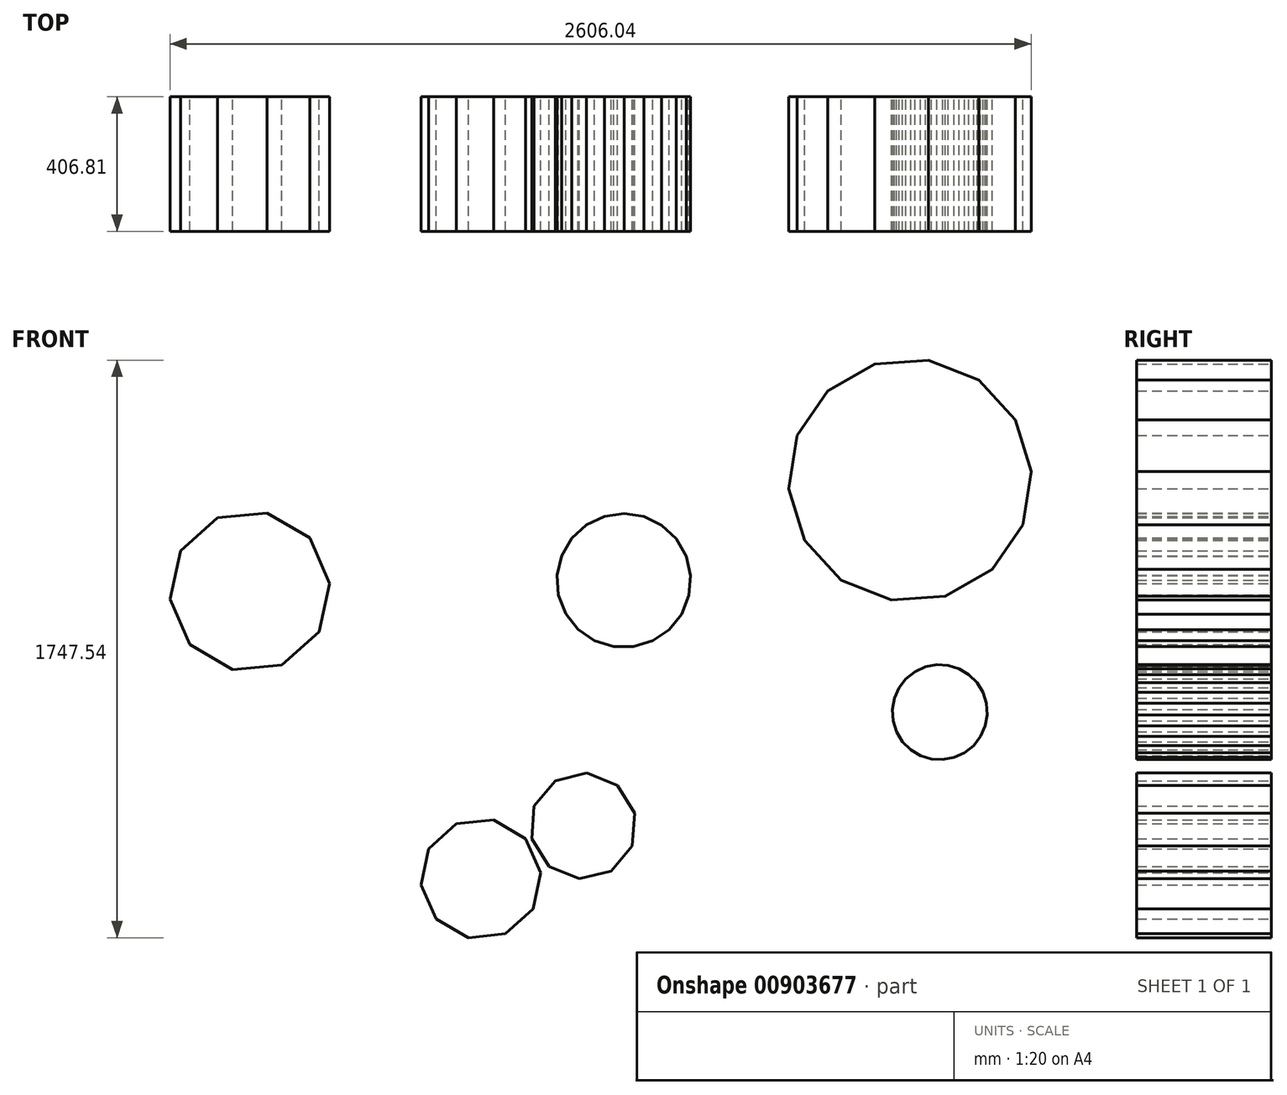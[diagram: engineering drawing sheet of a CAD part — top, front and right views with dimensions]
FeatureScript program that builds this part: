
annotation { "Feature Type Name" : "Feature", "Feature Type Description" : "" }
export const myFeature = defineFeature(function(context is Context, id is Id, definition is map)
    precondition{}
    {
        {
            var Q0;
            Q0=qCreatedBy(makeId("Front.planeOp"),FACE);
            var sketch = newSketch(context, id + "F0", { "sketchPlane" : qUnion([Q0])});
            skCircle(sketch, "E0.cCircle", {"center": v(340.3, -43.02) * mm, "radius": 160.48 * mm, "construction": true});
            skLineSegment(sketch, "E0.0", {"start": v(425.11, -179.25) * mm, "end": v(328.83, -203.09) * mm});
            skLineSegment(sketch, "E0.1", {"start": v(328.83, -203.09) * mm, "end": v(236.93, -165.78) * mm});
            skLineSegment(sketch, "E0.2", {"start": v(236.93, -165.78) * mm, "end": v(184.51, -81.58) * mm});
            skLineSegment(sketch, "E0.3", {"start": v(184.51, -81.58) * mm, "end": v(191.6, 17.35) * mm});
            skLineSegment(sketch, "E0.4", {"start": v(191.6, 17.35) * mm, "end": v(255.48, 93.22) * mm});
            skLineSegment(sketch, "E0.5", {"start": v(255.48, 93.22) * mm, "end": v(351.75, 117.06) * mm});
            skLineSegment(sketch, "E0.6", {"start": v(351.75, 117.06) * mm, "end": v(443.65, 79.75) * mm});
            skLineSegment(sketch, "E0.7", {"start": v(443.65, 79.75) * mm, "end": v(496.07, -4.45) * mm});
            skLineSegment(sketch, "E0.8", {"start": v(496.07, -4.45) * mm, "end": v(488.99, -103.38) * mm});
            skLineSegment(sketch, "E0.9", {"start": v(488.99, -103.38) * mm, "end": v(425.11, -179.25) * mm});
            skCircle(sketch, "E1.cCircle", {"center": v(30.75, -203.09) * mm, "radius": 182.11 * mm, "construction": true});
            skLineSegment(sketch, "E1.0", {"start": v(188.34, -294.35) * mm, "end": v(104.6, -369.55) * mm});
            skLineSegment(sketch, "E1.1", {"start": v(104.6, -369.55) * mm, "end": v(-7.35, -381.17) * mm});
            skLineSegment(sketch, "E1.2", {"start": v(-7.35, -381.17) * mm, "end": v(-104.75, -324.77) * mm});
            skLineSegment(sketch, "E1.3", {"start": v(-104.75, -324.77) * mm, "end": v(-150.39, -221.89) * mm});
            skLineSegment(sketch, "E1.4", {"start": v(-150.39, -221.89) * mm, "end": v(-126.85, -111.83) * mm});
            skLineSegment(sketch, "E1.5", {"start": v(-126.85, -111.83) * mm, "end": v(-43.1, -36.62) * mm});
            skLineSegment(sketch, "E1.6", {"start": v(-43.1, -36.62) * mm, "end": v(68.84, -25) * mm});
            skLineSegment(sketch, "E1.7", {"start": v(68.84, -25) * mm, "end": v(166.24, -81.4) * mm});
            skLineSegment(sketch, "E1.8", {"start": v(166.24, -81.4) * mm, "end": v(211.89, -184.29) * mm});
            skLineSegment(sketch, "E1.9", {"start": v(211.89, -184.29) * mm, "end": v(188.34, -294.35) * mm});
            skCircle(sketch, "E2.cCircle", {"center": v(-668.73, 666.87) * mm, "radius": 242.78 * mm, "construction": true});
            skLineSegment(sketch, "E2.0", {"start": v(-487.2, 828.1) * mm, "end": v(-427.1, 690.61) * mm});
            skLineSegment(sketch, "E2.1", {"start": v(-427.1, 690.61) * mm, "end": v(-459.3, 544.06) * mm});
            skLineSegment(sketch, "E2.2", {"start": v(-459.3, 544.06) * mm, "end": v(-571.48, 444.41) * mm});
            skLineSegment(sketch, "E2.3", {"start": v(-571.48, 444.41) * mm, "end": v(-720.81, 429.74) * mm});
            skLineSegment(sketch, "E2.4", {"start": v(-720.81, 429.74) * mm, "end": v(-850.25, 505.64) * mm});
            skLineSegment(sketch, "E2.5", {"start": v(-850.25, 505.64) * mm, "end": v(-910.35, 643.13) * mm});
            skLineSegment(sketch, "E2.6", {"start": v(-910.35, 643.13) * mm, "end": v(-878.16, 789.68) * mm});
            skLineSegment(sketch, "E2.7", {"start": v(-878.16, 789.68) * mm, "end": v(-765.97, 889.33) * mm});
            skLineSegment(sketch, "E2.8", {"start": v(-765.97, 889.33) * mm, "end": v(-616.64, 904) * mm});
            skLineSegment(sketch, "E2.9", {"start": v(-616.64, 904) * mm, "end": v(-487.2, 828.1) * mm});
            skCircle(sketch, "E3.cCircle", {"center": v(1329.22, 1003.32) * mm, "radius": 367.39 * mm, "construction": true});
            skLineSegment(sketch, "E3.0", {"start": v(1272.95, 640.27) * mm, "end": v(1121, 700.63) * mm});
            skLineSegment(sketch, "E3.1", {"start": v(1121, 700.63) * mm, "end": v(1010.3, 820.95) * mm});
            skLineSegment(sketch, "E3.2", {"start": v(1010.3, 820.95) * mm, "end": v(962.75, 977.39) * mm});
            skLineSegment(sketch, "E3.3", {"start": v(962.75, 977.39) * mm, "end": v(987.8, 1138.96) * mm});
            skLineSegment(sketch, "E3.4", {"start": v(987.8, 1138.96) * mm, "end": v(1080.46, 1273.67) * mm});
            skLineSegment(sketch, "E3.5", {"start": v(1080.46, 1273.67) * mm, "end": v(1222.4, 1354.83) * mm});
            skLineSegment(sketch, "E3.6", {"start": v(1222.4, 1354.83) * mm, "end": v(1385.5, 1366.37) * mm});
            skLineSegment(sketch, "E3.7", {"start": v(1385.5, 1366.37) * mm, "end": v(1537.44, 1306) * mm});
            skLineSegment(sketch, "E3.8", {"start": v(1537.44, 1306) * mm, "end": v(1648.15, 1185.68) * mm});
            skLineSegment(sketch, "E3.9", {"start": v(1648.15, 1185.68) * mm, "end": v(1695.7, 1029.24) * mm});
            skLineSegment(sketch, "E3.10", {"start": v(1695.7, 1029.24) * mm, "end": v(1670.65, 867.67) * mm});
            skLineSegment(sketch, "E3.11", {"start": v(1670.65, 867.67) * mm, "end": v(1577.98, 732.96) * mm});
            skLineSegment(sketch, "E3.12", {"start": v(1577.98, 732.96) * mm, "end": v(1436.05, 651.8) * mm});
            skLineSegment(sketch, "E3.13", {"start": v(1436.05, 651.8) * mm, "end": v(1272.95, 640.27) * mm});
            skCircle(sketch, "E4.cCircle", {"center": v(463.14, 699.88) * mm, "radius": 202.49 * mm, "construction": true});
            skLineSegment(sketch, "E4.0", {"start": v(665.12, 714.22) * mm, "end": v(660.37, 654.05) * mm});
            skLineSegment(sketch, "E4.1", {"start": v(660.37, 654.05) * mm, "end": v(638.1, 597.95) * mm});
            skLineSegment(sketch, "E4.2", {"start": v(638.1, 597.95) * mm, "end": v(600.28, 550.9) * mm});
            skLineSegment(sketch, "E4.3", {"start": v(600.28, 550.9) * mm, "end": v(550.27, 517.1) * mm});
            skLineSegment(sketch, "E4.4", {"start": v(550.27, 517.1) * mm, "end": v(492.53, 499.54) * mm});
            skLineSegment(sketch, "E4.5", {"start": v(492.53, 499.54) * mm, "end": v(432.17, 499.78) * mm});
            skLineSegment(sketch, "E4.6", {"start": v(432.17, 499.78) * mm, "end": v(374.56, 517.8) * mm});
            skLineSegment(sketch, "E4.7", {"start": v(374.56, 517.8) * mm, "end": v(324.83, 552) * mm});
            skLineSegment(sketch, "E4.8", {"start": v(324.83, 552) * mm, "end": v(287.38, 599.33) * mm});
            skLineSegment(sketch, "E4.9", {"start": v(287.38, 599.33) * mm, "end": v(265.55, 655.6) * mm});
            skLineSegment(sketch, "E4.10", {"start": v(265.55, 655.6) * mm, "end": v(261.28, 715.81) * mm});
            skLineSegment(sketch, "E4.11", {"start": v(261.28, 715.81) * mm, "end": v(274.94, 774.6) * mm});
            skLineSegment(sketch, "E4.12", {"start": v(274.94, 774.6) * mm, "end": v(305.33, 826.76) * mm});
            skLineSegment(sketch, "E4.13", {"start": v(305.33, 826.76) * mm, "end": v(349.73, 867.64) * mm});
            skLineSegment(sketch, "E4.14", {"start": v(349.73, 867.64) * mm, "end": v(404.22, 893.6) * mm});
            skLineSegment(sketch, "E4.15", {"start": v(404.22, 893.6) * mm, "end": v(463.94, 902.37) * mm});
            skLineSegment(sketch, "E4.16", {"start": v(463.94, 902.37) * mm, "end": v(523.59, 893.14) * mm});
            skLineSegment(sketch, "E4.17", {"start": v(523.59, 893.14) * mm, "end": v(577.86, 866.74) * mm});
            skLineSegment(sketch, "E4.18", {"start": v(577.86, 866.74) * mm, "end": v(621.95, 825.5) * mm});
            skLineSegment(sketch, "E4.19", {"start": v(621.95, 825.5) * mm, "end": v(651.92, 773.12) * mm});
            skLineSegment(sketch, "E4.20", {"start": v(651.92, 773.12) * mm, "end": v(665.12, 714.22) * mm});
            skCircle(sketch, "E5.cCircle", {"center": v(1419.45, 301.15) * mm, "radius": 143.93 * mm, "construction": true});
            skLineSegment(sketch, "E5.0", {"start": v(1428.9, 157.53) * mm, "end": v(1394.25, 159.45) * mm});
            skLineSegment(sketch, "E5.1", {"start": v(1394.25, 159.45) * mm, "end": v(1361.07, 169.6) * mm});
            skLineSegment(sketch, "E5.2", {"start": v(1361.07, 169.6) * mm, "end": v(1331.28, 187.4) * mm});
            skLineSegment(sketch, "E5.3", {"start": v(1331.28, 187.4) * mm, "end": v(1306.62, 211.8) * mm});
            skLineSegment(sketch, "E5.4", {"start": v(1306.62, 211.8) * mm, "end": v(1288.51, 241.4) * mm});
            skLineSegment(sketch, "E5.5", {"start": v(1288.51, 241.4) * mm, "end": v(1278.02, 274.47) * mm});
            skLineSegment(sketch, "E5.6", {"start": v(1278.02, 274.47) * mm, "end": v(1275.74, 309.09) * mm});
            skLineSegment(sketch, "E5.7", {"start": v(1275.74, 309.09) * mm, "end": v(1281.82, 343.25) * mm});
            skLineSegment(sketch, "E5.8", {"start": v(1281.82, 343.25) * mm, "end": v(1295.9, 374.96) * mm});
            skLineSegment(sketch, "E5.9", {"start": v(1295.9, 374.96) * mm, "end": v(1317.15, 402.39) * mm});
            skLineSegment(sketch, "E5.10", {"start": v(1317.15, 402.39) * mm, "end": v(1344.35, 423.93) * mm});
            skLineSegment(sketch, "E5.11", {"start": v(1344.35, 423.93) * mm, "end": v(1375.91, 438.33) * mm});
            skLineSegment(sketch, "E5.12", {"start": v(1375.91, 438.33) * mm, "end": v(1410, 444.77) * mm});
            skLineSegment(sketch, "E5.13", {"start": v(1410, 444.77) * mm, "end": v(1444.65, 442.85) * mm});
            skLineSegment(sketch, "E5.14", {"start": v(1444.65, 442.85) * mm, "end": v(1477.83, 432.7) * mm});
            skLineSegment(sketch, "E5.15", {"start": v(1477.83, 432.7) * mm, "end": v(1507.62, 414.9) * mm});
            skLineSegment(sketch, "E5.16", {"start": v(1507.62, 414.9) * mm, "end": v(1532.28, 390.5) * mm});
            skLineSegment(sketch, "E5.17", {"start": v(1532.28, 390.5) * mm, "end": v(1550.38, 360.9) * mm});
            skLineSegment(sketch, "E5.18", {"start": v(1550.38, 360.9) * mm, "end": v(1560.88, 327.83) * mm});
            skLineSegment(sketch, "E5.19", {"start": v(1560.88, 327.83) * mm, "end": v(1563.16, 293.21) * mm});
            skLineSegment(sketch, "E5.20", {"start": v(1563.16, 293.21) * mm, "end": v(1557.08, 259.05) * mm});
            skLineSegment(sketch, "E5.21", {"start": v(1557.08, 259.05) * mm, "end": v(1543, 227.34) * mm});
            skLineSegment(sketch, "E5.22", {"start": v(1543, 227.34) * mm, "end": v(1521.75, 199.91) * mm});
            skLineSegment(sketch, "E5.23", {"start": v(1521.75, 199.91) * mm, "end": v(1494.55, 178.37) * mm});
            skLineSegment(sketch, "E5.24", {"start": v(1494.55, 178.37) * mm, "end": v(1462.99, 163.97) * mm});
            skLineSegment(sketch, "E5.25", {"start": v(1462.99, 163.97) * mm, "end": v(1428.9, 157.53) * mm});
            skSolve(sketch);
        }
        {
            var Q0;
            Q0 = qSketchRegion(id + "F0", true);
            extrude(context, id + "F1", {"entities" : qUnion([Q0]), "depth" : 406.8 * mm, "offsetDistance" : 25.4 * mm});
        }
    });
